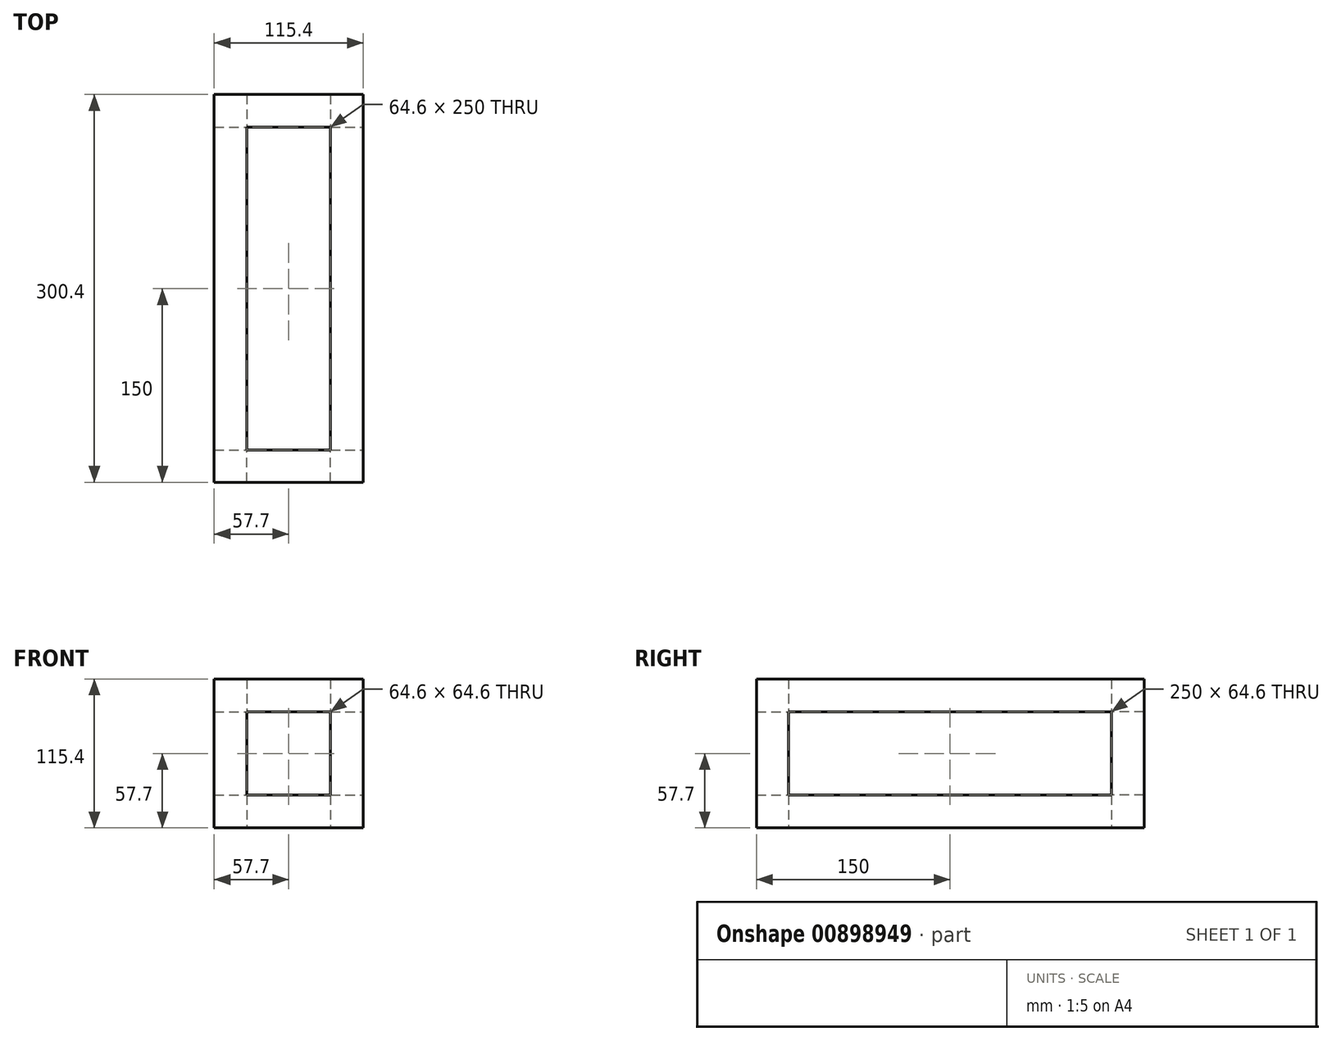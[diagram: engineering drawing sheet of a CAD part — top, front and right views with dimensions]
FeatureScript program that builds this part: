
annotation { "Feature Type Name" : "Feature", "Feature Type Description" : "" }
export const myFeature = defineFeature(function(context is Context, id is Id, definition is map)
    precondition{}
    {
        {
            var Q0;
            Q0=qCreatedBy(makeId("Front.planeOp"),FACE);
            var sketch = newSketch(context, id + "F0", { "sketchPlane" : qUnion([Q0])});
            skLineSegment(sketch, "E0.bottom", {"start": v(-57.7, 57.7) * mm, "end": v(-32.3, 57.7) * mm});
            skLineSegment(sketch, "E0.top", {"start": v(-57.7, 32.3) * mm, "end": v(-32.3, 32.3) * mm});
            skLineSegment(sketch, "E0.left", {"start": v(-57.7, 57.7) * mm, "end": v(-57.7, 32.3) * mm});
            skLineSegment(sketch, "E0.right", {"start": v(-32.3, 57.7) * mm, "end": v(-32.3, 32.3) * mm});
            skLineSegment(sketch, "E1.0.1.0", {"start": v(-57.7, -32.3) * mm, "end": v(-32.3, -32.3) * mm});
            skLineSegment(sketch, "E1.0.1.1", {"start": v(-57.7, -32.3) * mm, "end": v(-57.7, -57.7) * mm});
            skLineSegment(sketch, "E1.0.1.2", {"start": v(-57.7, -57.7) * mm, "end": v(-32.3, -57.7) * mm});
            skLineSegment(sketch, "E1.0.1.3", {"start": v(-32.3, -32.3) * mm, "end": v(-32.3, -57.7) * mm});
            skLineSegment(sketch, "E1.1.0.0", {"start": v(32.3, 57.7) * mm, "end": v(57.7, 57.7) * mm});
            skLineSegment(sketch, "E1.1.0.1", {"start": v(32.3, 57.7) * mm, "end": v(32.3, 32.3) * mm});
            skLineSegment(sketch, "E1.1.0.2", {"start": v(32.3, 32.3) * mm, "end": v(57.7, 32.3) * mm});
            skLineSegment(sketch, "E1.1.0.3", {"start": v(57.7, 57.7) * mm, "end": v(57.7, 32.3) * mm});
            skLineSegment(sketch, "E1.1.1.0", {"start": v(32.3, -32.3) * mm, "end": v(57.7, -32.3) * mm});
            skLineSegment(sketch, "E1.1.1.1", {"start": v(32.3, -32.3) * mm, "end": v(32.3, -57.7) * mm});
            skLineSegment(sketch, "E1.1.1.2", {"start": v(32.3, -57.7) * mm, "end": v(57.7, -57.7) * mm});
            skLineSegment(sketch, "E1.1.1.3", {"start": v(57.7, -32.3) * mm, "end": v(57.7, -57.7) * mm});
            skLineSegment(sketch, "E1.direction1", {"start": v(-57.7, 57.7) * mm, "end": v(32.3, 57.7) * mm, "construction": true});
            skLineSegment(sketch, "E1.direction2", {"start": v(-57.7, 57.7) * mm, "end": v(-57.7, -32.3) * mm, "construction": true});
            skSolve(sketch);
        }
        {
            var Q0;
            Q0=qCreatedBy(makeId("Front.planeOp"),FACE);
            var sketch = newSketch(context, id + "F1", { "sketchPlane" : qUnion([Q0])});
            skLineSegment(sketch, "E2.bottom", {"start": v(57.7, 57.7) * mm, "end": v(-57.7, 57.7) * mm});
            skLineSegment(sketch, "E2.top", {"start": v(57.7, -57.7) * mm, "end": v(-57.7, -57.7) * mm});
            skLineSegment(sketch, "E2.left", {"start": v(57.7, 57.7) * mm, "end": v(57.7, -57.7) * mm});
            skLineSegment(sketch, "E2.right", {"start": v(-57.7, 57.7) * mm, "end": v(-57.7, -57.7) * mm});
            skLineSegment(sketch, "E3.bottom", {"start": v(32.3, 32.3) * mm, "end": v(-32.3, 32.3) * mm});
            skLineSegment(sketch, "E3.top", {"start": v(32.3, -32.3) * mm, "end": v(-32.3, -32.3) * mm});
            skLineSegment(sketch, "E3.left", {"start": v(32.3, 32.3) * mm, "end": v(32.3, -32.3) * mm});
            skLineSegment(sketch, "E3.right", {"start": v(-32.3, 32.3) * mm, "end": v(-32.3, -32.3) * mm});
            skSolve(sketch);
        }
        {
            var Q0;
            Q0=makeQuery(id+"F1.imprint","IMPRINT",FACE,{"disambiguationData":[TD([[makeQuery(id+"F1.imprint","IMPRINT",EDGE,{"derivedFrom":sQuery(id+"F1.wireOp",EDGE,"E2.bottom")}),1.0]])]});
            extrude(context, id + "F2", {"entities" : qUnion([Q0]), "oppositeDirection" : true, "depth" : 25.4 * mm, "offsetDistance" : 25 * mm});
        }
        {
            var Q0;
            Q0=makeQuery(id+"F0.imprint","IMPRINT",FACE,{"disambiguationData":[TD([[makeQuery(id+"F0.imprint","IMPRINT",EDGE,{"derivedFrom":sQuery(id+"F0.wireOp",EDGE,"E1.1.0.0")}),-1.0]])]});
            var Q1;
            Q1=makeQuery(id+"F0.imprint","IMPRINT",FACE,{"disambiguationData":[TD([[makeQuery(id+"F0.imprint","IMPRINT",EDGE,{"derivedFrom":sQuery(id+"F0.wireOp",EDGE,"E0.bottom")}),-1.0]])]});
            var Q2;
            Q2=makeQuery(id+"F0.imprint","IMPRINT",FACE,{"disambiguationData":[TD([[makeQuery(id+"F0.imprint","IMPRINT",EDGE,{"derivedFrom":sQuery(id+"F0.wireOp",EDGE,"E1.0.1.0")}),-1.0]])]});
            var Q3;
            Q3=makeQuery(id+"F0.imprint","IMPRINT",FACE,{"disambiguationData":[TD([[makeQuery(id+"F0.imprint","IMPRINT",EDGE,{"derivedFrom":sQuery(id+"F0.wireOp",EDGE,"E1.1.1.0")}),-1.0]])]});
            extrude(context, id + "F3", {"entities" : qUnion([Q0, Q1, Q2, Q3]), "operationType" : NewBodyOperationType.ADD, "depth" : 250 * mm, "offsetDistance" : 25 * mm});
        }
        {
            var Q0;
            Q0=makeQuery(id+"F3.opExtrude","CAP_FACE",FACE,{"disambiguationData":[OSD([sQuery(id+"F0.wireOp",EDGE,"E0.bottom"),sQuery(id+"F0.wireOp",EDGE,"E0.top"),sQuery(id+"F0.wireOp",EDGE,"E0.left"),sQuery(id+"F0.wireOp",EDGE,"E0.right")])],"isStart":false});
            var sketch = newSketch(context, id + "F4", { "sketchPlane" : qUnion([Q0])});
            skLineSegment(sketch, "E4.bottom", {"start": v(-57.7, 57.7) * mm, "end": v(57.7, 57.7) * mm});
            skLineSegment(sketch, "E4.top", {"start": v(-57.7, -57.7) * mm, "end": v(57.7, -57.7) * mm});
            skLineSegment(sketch, "E4.left", {"start": v(-57.7, 57.7) * mm, "end": v(-57.7, -57.7) * mm});
            skLineSegment(sketch, "E4.right", {"start": v(57.7, 57.7) * mm, "end": v(57.7, -57.7) * mm});
            skLineSegment(sketch, "E5.bottom", {"start": v(-32.3, 32.3) * mm, "end": v(32.3, 32.3) * mm});
            skLineSegment(sketch, "E5.top", {"start": v(-32.3, -32.3) * mm, "end": v(32.3, -32.3) * mm});
            skLineSegment(sketch, "E5.left", {"start": v(-32.3, 32.3) * mm, "end": v(-32.3, -32.3) * mm});
            skLineSegment(sketch, "E5.right", {"start": v(32.3, 32.3) * mm, "end": v(32.3, -32.3) * mm});
            skSolve(sketch);
        }
        {
            var Q0;
            {var subQ4=makeQuery(id+"F3.opExtrude","CAP_EDGE",EDGE,{"disambiguationData":[OSD([sQuery(id+"F0.wireOp",EDGE,"E0.top")])],"isStart":false});Q0=makeQuery(id+"F4.imprint","IMPRINT",FACE,{"disambiguationData":[TD([[makeQuery(id+"F4.imprint","IMPRINT",EDGE,{"derivedFrom":subQ4}),1.0]])]});}
            var Q1;
            {var subQ2=sQuery(id+"F4.wireOp",EDGE,"E4.top");Q1=makeQuery(id+"F4.imprint","IMPRINT",FACE,{"disambiguationData":[TD([[makeQuery(id+"F4.imprint","IMPRINT",EDGE,{"derivedFrom":subQ2}),1.0]])]});}
            extrude(context, id + "F5", {"entities" : qUnion([Q0, Q1]), "operationType" : NewBodyOperationType.ADD, "depth" : 25 * mm, "offsetDistance" : 25 * mm});
        }
    });
